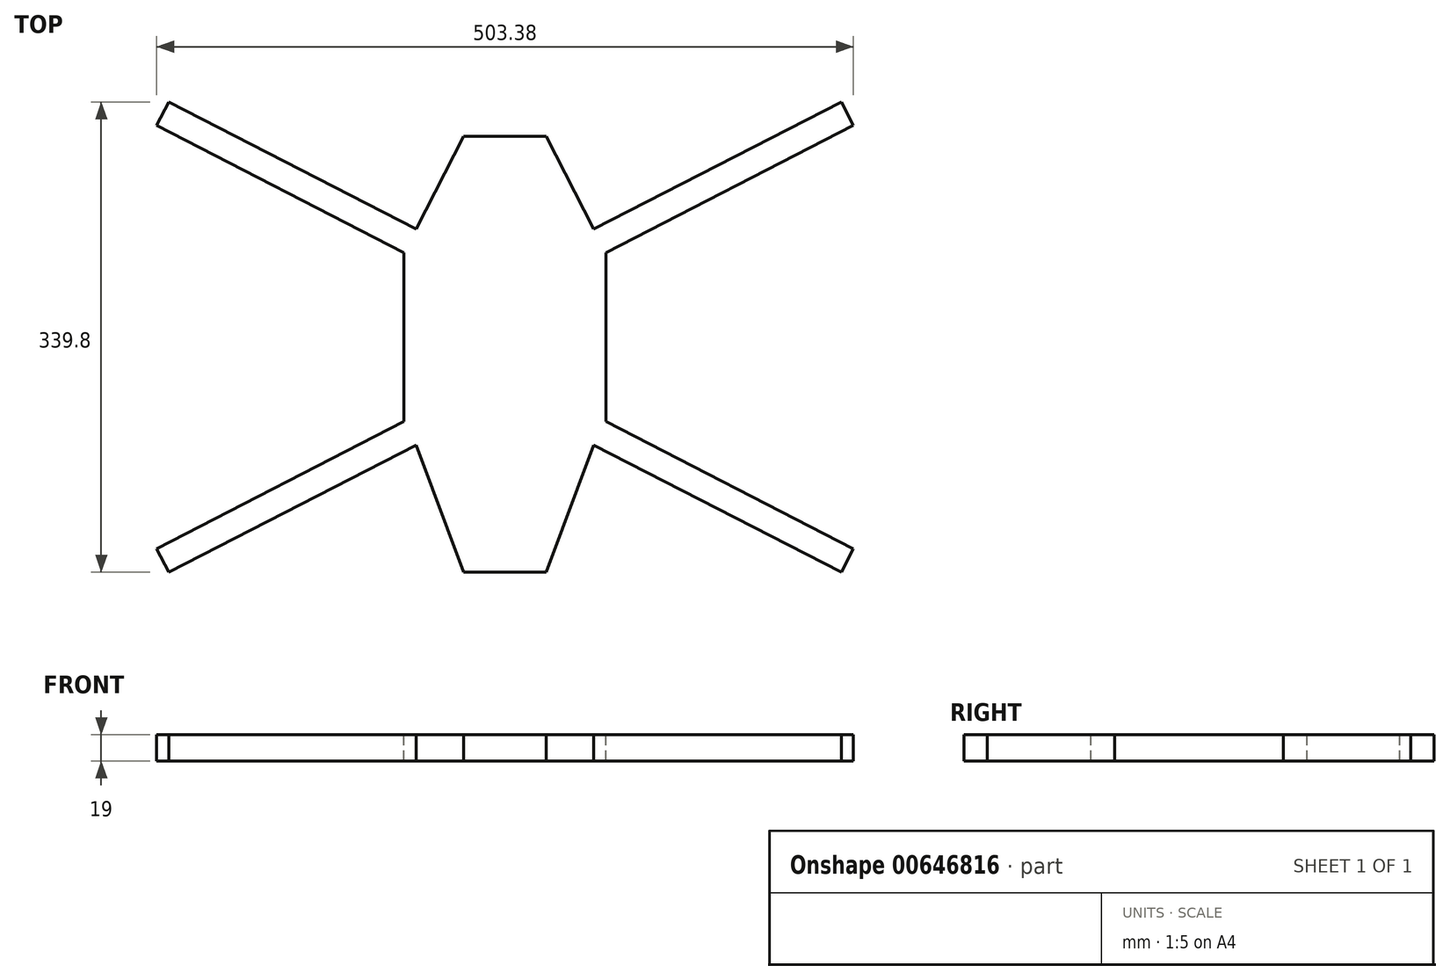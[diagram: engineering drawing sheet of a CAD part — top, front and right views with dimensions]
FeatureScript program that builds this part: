
annotation { "Feature Type Name" : "Feature", "Feature Type Description" : "" }
export const myFeature = defineFeature(function(context is Context, id is Id, definition is map)
    precondition{}
    {
        {
            var Q0;
            Q0=qCreatedBy(makeId("Top.planeOp"),FACE);
            var sketch = newSketch(context, id + "F0", { "sketchPlane" : qUnion([Q0])});
            skLineSegment(sketch, "E0", {"start": v(0, 0) * mm, "end": v(0, 200.14) * mm, "construction": true});
            skLineSegment(sketch, "E1", {"start": v(0, 0) * mm, "end": v(-120.89, 0) * mm, "construction": true});
            skLineSegment(sketch, "E2", {"start": v(-243, 169.9) * mm, "end": v(-251.69, 153) * mm});
            skLineSegment(sketch, "E3", {"start": v(-251.69, 153) * mm, "end": v(-72.93, 61.1) * mm});
            skLineSegment(sketch, "E4", {"start": v(-243, 169.9) * mm, "end": v(-64.24, 78) * mm});
            skLineSegment(sketch, "E5", {"start": v(-247.34, 161.45) * mm, "end": v(0, 34.28) * mm, "construction": true});
            skLineSegment(sketch, "E6.MirrorCS", {"start": v(-251.69, -153) * mm, "end": v(-72.93, -61.1) * mm});
            skLineSegment(sketch, "E7.MirrorCS", {"start": v(-243, -169.9) * mm, "end": v(-251.69, -153) * mm});
            skLineSegment(sketch, "E8.MirrorCS", {"start": v(-243, -169.9) * mm, "end": v(-64.24, -78) * mm});
            skLineSegment(sketch, "E9.MirrorCS", {"start": v(243, 169.9) * mm, "end": v(64.24, 78) * mm});
            skLineSegment(sketch, "E10.MirrorCS", {"start": v(243, 169.9) * mm, "end": v(251.69, 153) * mm});
            skLineSegment(sketch, "E11.MirrorCS", {"start": v(251.69, 153) * mm, "end": v(72.93, 61.1) * mm});
            skPoint(sketch, "E12", {"position": v(-129.28, 100.75) * mm});
            skLineSegment(sketch, "E13.MirrorCS", {"start": v(243, -169.9) * mm, "end": v(251.69, -153) * mm});
            skLineSegment(sketch, "E14.MirrorCS", {"start": v(251.69, -153) * mm, "end": v(72.93, -61.1) * mm});
            skLineSegment(sketch, "E15.MirrorCS", {"start": v(243, -169.9) * mm, "end": v(64.24, -78) * mm});
            skLineSegment(sketch, "E16", {"start": v(-72.93, 61.1) * mm, "end": v(-72.93, -61.1) * mm});
            skLineSegment(sketch, "E17", {"start": v(72.93, -61.1) * mm, "end": v(72.93, 61.1) * mm});
            skLineSegment(sketch, "E18", {"start": v(-64.24, 78) * mm, "end": v(-29.74, 145.1) * mm});
            skLineSegment(sketch, "E19", {"start": v(-29.74, 145.1) * mm, "end": v(0, 145.1) * mm});
            skLineSegment(sketch, "E20", {"start": v(-64.24, -78) * mm, "end": v(-29.74, -169.9) * mm});
            skLineSegment(sketch, "E21", {"start": v(-29.74, -169.9) * mm, "end": v(0, -169.9) * mm});
            skLineSegment(sketch, "E22.MirrorCS", {"start": v(29.74, 145.1) * mm, "end": v(0, 145.1) * mm});
            skLineSegment(sketch, "E23.MirrorCS", {"start": v(64.24, 78) * mm, "end": v(29.74, 145.1) * mm});
            skLineSegment(sketch, "E24.MirrorCS", {"start": v(64.24, -78) * mm, "end": v(29.74, -169.9) * mm});
            skLineSegment(sketch, "E25.MirrorCS", {"start": v(29.74, -169.9) * mm, "end": v(0, -169.9) * mm});
            skSolve(sketch);
        }
        {
            var Q0;
            Q0=qSketchRegion(id+"F0",true);
            extrude(context, id + "F1", {"entities" : qUnion([Q0]), "oppositeDirection" : true, "depth" : 19 * mm});
        }
    });
